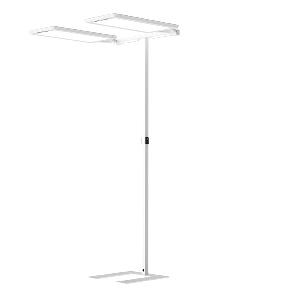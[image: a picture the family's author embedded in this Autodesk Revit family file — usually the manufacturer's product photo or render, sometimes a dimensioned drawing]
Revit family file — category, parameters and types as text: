
# Revit family: yara_doubleu_-_yus_2_15000_840_rx_ws_cee_s0_c_114268000-00812894_1cde
name_source: partatom
category: Lighting Fixtures
units: mm (PartAtom-declared; Revit-internal decimal feet)

## family parameters
Cut with Voids When Loaded = No
Host = Face
Light Source = No
Part Type = Normal
Room Calculation Point = No
Round Connector Dimension = Use Diameter
Shared = No

## types (1)
- YARA.doubleU - YUS 2/15000/840/RX/WS/CEE/S0/C (1 x LED, 15000 lm, 4000K)
    Apparent Load = 214 VA
    Approval mark = CE
    CIE Flux Codes = 58 87 97 13 100
    Color Rendering = 80-89
    Color Temperature = 4000K
    Control Gear = Electronic ballast
    Default Elevation = 1800 mm
    Description = YUS 2/15000/840/RX/WS/CEE/S0/C|Free-standing luminaire|light source: LED Cold white   |work equipment: Electronic ballast DALI|connected load: 220-240 V, 50/60 Hz|Power consumption: approx. 210 W|power factor: approx. 0,966|luminous flux: 30000 lm|luminous efficacy: 142 lm/W|light distribution: Direct/indirect|direct ratio: approx. 13 %|color rendering index (CRI): >= 80|chromaticity tolerance:  3 SDCM|technology: Multiple daylight-dependent motion sensors|operation: Wireless switch|luminaire body|material: Aluminium/plastic|surface: Powder coatet|colour: White|lamp cover: Acrylic (PMMA)|tubular section|material: Steel tube|surface: Powder-coated|Form: Tubular section upright|colour of tubular section: White|luminaire base|Form: C-form flat|weight (net): approx. 26.0 kg|mains lead: 3.00 m Mains plug CEE 7/VII|Fastening: Floor standing base|glare control: Conical prismatic screen|luminance(L65): <= 2700 cd/m|unified glare rating(4H 8H): <=  16|special features: App control, Asymmetric radiation, Direct and indirect lighting component with edge light and light guidetechnology for a homogeneous light exit, Flicker-free, LTX multisensor for workplace optimisation, Magnetic control panel, freely positionable, Optional LTX Cloud connection, TALK Bluetooth|Approval mark: VDE - ENEC|
    Frequency = 50 Hz, 60 Hz
    Height = 24 mm  [stored 0.0787402 ft]
    Lamp = 1 x LED
    Lamp Light Flux = 15000 lm
    Lamp count = 1
    Length = 690 mm
    Luminous efficacy = 140 lm/W
    Manufacturer = Waldmann
    ModVariant = No
    Model = 114268000-00812894
    Mounting Place = Floor
    Mounting Type = Freestanding
    Number of Poles = 1
    OnlyDefault = Yes
    Power Factor = 1
    Product Name = YARA.doubleU - YUS 2/15000/840/RX/WS/CEE/S0/C
    Product group = Free standing luminaire
    ProductGroupID = 13
    Protection Class = Protection class I
    Protection Degree = IP 20
    RLX_Detail_Level = 1
    RlxData = <blob elided: 67521 chars, md5=af5720dc>
    Socket = socket
    Standby Power = 0 W
    System Light Flux = 30000 lm
    System Power = 214 W
    Type Comments = Product without accessories
    Type Image = yus-rx-ws-c.jpg
    URL = http://relux.com
    VarID = ---
    Voltage = 230 V
    Voltage Range = 220-240 V
    Weight = 0.00 kg
    Width = 358 mm

note: [stored X ft] marks values corroborated as IEEE doubles in the binary element streams (Revit-internal decimal feet)

## geometry (parser evidence)
native form markers: Blend x4, Sweep x17
no freeform markers — native parametric forms only
